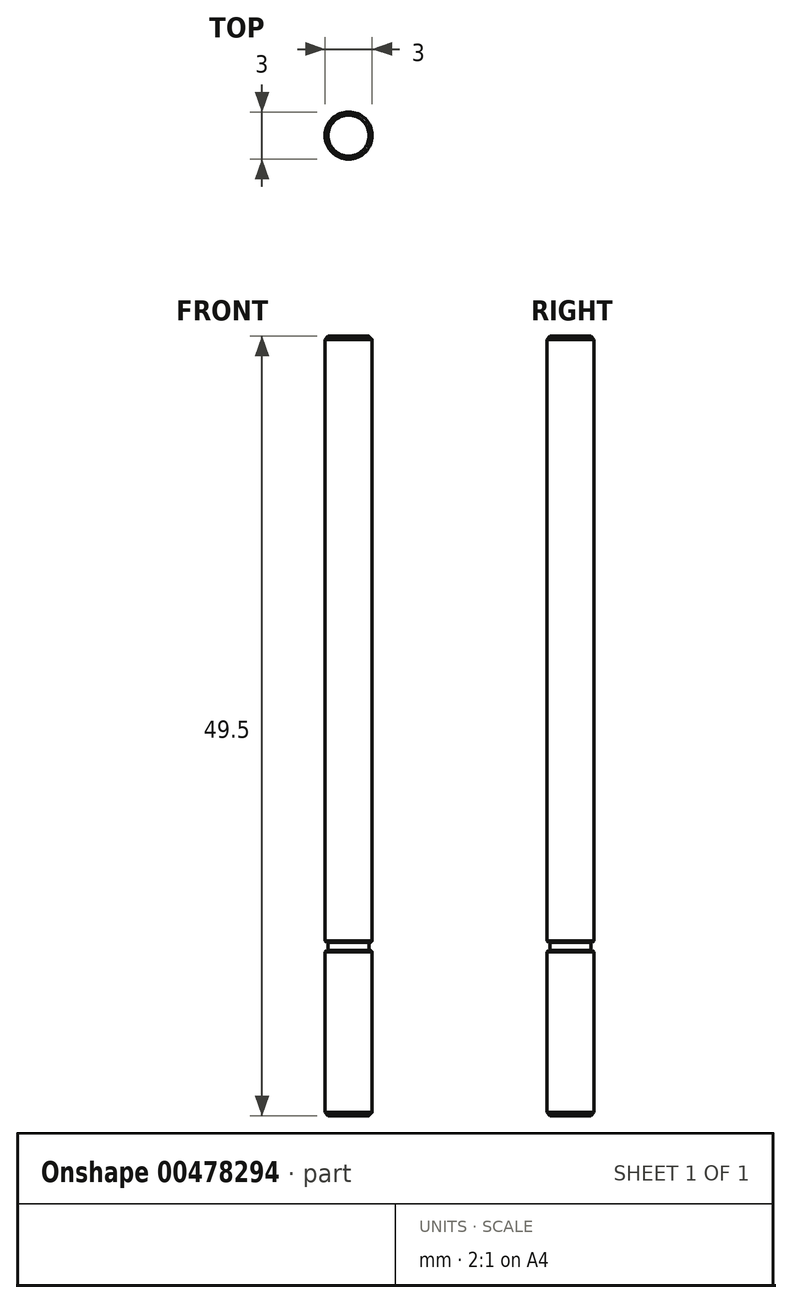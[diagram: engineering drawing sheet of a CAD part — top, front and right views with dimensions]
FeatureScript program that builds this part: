
annotation { "Feature Type Name" : "Feature", "Feature Type Description" : "" }
export const myFeature = defineFeature(function(context is Context, id is Id, definition is map)
    precondition{}
    {
        {
            var Q0;
            Q0=qCreatedBy(makeId("Top.planeOp"),FACE);
            var sketch = newSketch(context, id + "F0", { "sketchPlane" : qUnion([Q0])});
            skCircle(sketch, "E0", {"center": v(0, 0) * mm, "radius": 1.5 * mm});
            skCircle(sketch, "E1.0", {"center": v(0, 0) * mm, "radius": 1.3 * mm});
            skSolve(sketch);
        }
        {
            var Q0;
            Q0=qSketchRegion(id+"F0",true);
            var Q1;
            Q1=makeQuery(id+"F0.imprint","IMPRINT",FACE,{"disambiguationData":[TD([[makeQuery(id+"F0.imprint","IMPRINT",EDGE,{"derivedFrom":sQuery(id+"F0.wireOp",EDGE,"E1.0")}),1.0]])]});
            extrude(context, id + "F1", {"entities" : qUnion([Q0, Q1]), "depth" : 38.5 * mm});
        }
        {
            var Q0;
            Q0=makeQuery(id+"F0.imprint","IMPRINT",FACE,{"disambiguationData":[TD([[makeQuery(id+"F0.imprint","IMPRINT",EDGE,{"derivedFrom":sQuery(id+"F0.wireOp",EDGE,"E1.0")}),1.0]])]});
            extrude(context, id + "F2", {"entities" : qUnion([Q0]), "operationType" : NewBodyOperationType.ADD, "oppositeDirection" : true, "depth" : 1 * mm});
        }
        {
            var Q0;
            Q0=qSketchRegion(id+"F0",true);
            extrude(context, id + "F3", {"entities" : qUnion([Q0]), "operationType" : NewBodyOperationType.ADD, "oppositeDirection" : true, "depth" : 1 * mm, "hasSecondDirection" : true, "secondDirectionOppositeDirection" : true, "secondDirectionDepth" : 0.5 * mm});
        }
        {
            var Q0;
            {var subQ0=sQuery(id+"F0.wireOp",EDGE,"E1.0");Q0=makeQuery(id+"F3.boolean.opBoolean","MERGE",FACE,{"derivedFrom":[makeQuery(id+"F2.opExtrude","CAP_FACE",FACE,{"disambiguationData":[OSD([subQ0])],"isStart":false}),makeQuery(id+"F3.opExtrude","CAP_FACE",FACE,{"disambiguationData":[OSD([sQuery(id+"F0.wireOp",EDGE,"E0"),subQ0])],"isStart":false})]});}
            extrude(context, id + "F4", {"entities" : qUnion([Q0]), "operationType" : NewBodyOperationType.ADD, "depth" : 10 * mm});
        }
        {
            var Q0;
            Q0=makeQuery(id+"F1.opExtrude","CAP_EDGE",EDGE,{"disambiguationData":[OSD([sQuery(id+"F0.wireOp",EDGE,"E0")])],"isStart":false});
            var Q1;
            Q1=makeQuery(id+"F4.opExtrude","CAP_EDGE",EDGE,{"disambiguationData":[OSD([sQuery(id+"F0.wireOp",EDGE,"E0")])],"isStart":false});
            chamfer(context, id + "F5", {"entities" : qUnion([Q0, Q1]), "width" : 0.2 * mm, "tangentPropagation" : true});
        }
        {
            var Q0;
            Q0=makeQuery(id+"F3.opExtrude","CAP_EDGE",EDGE,{"disambiguationData":[OSD([sQuery(id+"F0.wireOp",EDGE,"E0")])],"isStart":true});
            var Q1;
            Q1=makeQuery(id+"F1.opExtrude","CAP_EDGE",EDGE,{"disambiguationData":[OSD([sQuery(id+"F0.wireOp",EDGE,"E0")])],"isStart":true});
            chamfer(context, id + "F6", {"entities" : qUnion([Q0, Q1]), "width" : 0.1 * mm, "tangentPropagation" : true});
        }
    });
